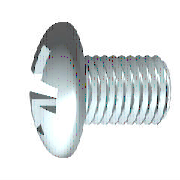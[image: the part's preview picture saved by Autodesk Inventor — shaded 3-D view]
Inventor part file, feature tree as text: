
AUTODESK INVENTOR PART (.ipt)
format: ipt  version: 2020 (Build 240168000, 168)  size: 274,432 bytes
history: native  units: mm (DEFAULTED — no unit token found)
features: extrude x1, other x1, plane x1
ambient origin geometry x7: Origin, YZ Plane, XZ Plane, X Axis, Y Axis, Z Axis, Center Point
bodies: Solid1 (feature_tree), Body (feature_tree)
feature tree (3):
  extrude  "Slot"  Depth=2.0mm
  other  "Cut"
  plane  "Work Plane3"
